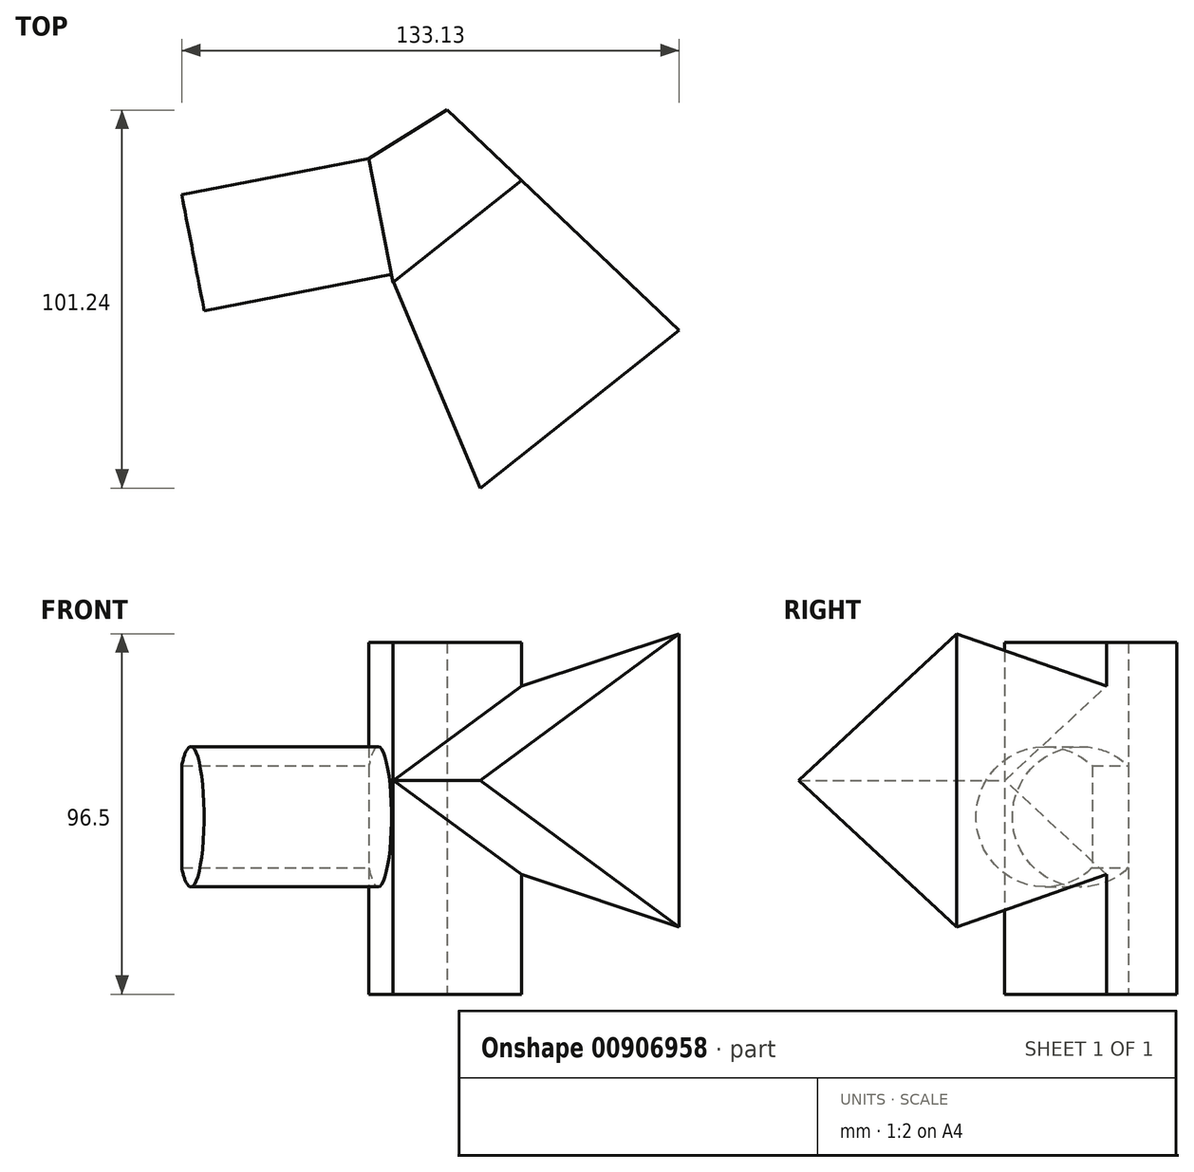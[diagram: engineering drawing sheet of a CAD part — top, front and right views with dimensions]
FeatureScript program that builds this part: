
annotation { "Feature Type Name" : "Feature", "Feature Type Description" : "" }
export const myFeature = defineFeature(function(context is Context, id is Id, definition is map)
    precondition{}
    {
        {
            var Q0;
            Q0=qCreatedBy(makeId("Top.planeOp"),FACE);
            var sketch = newSketch(context, id + "F0", { "sketchPlane" : qUnion([Q0])});
            skLineSegment(sketch, "E0", {"start": v(-14.54, -24.13) * mm, "end": v(-20.96, 9.05) * mm});
            skLineSegment(sketch, "E1", {"start": v(-20.96, 9.05) * mm, "end": v(0, 22.03) * mm});
            skLineSegment(sketch, "E2", {"start": v(-14.54, -24.13) * mm, "end": v(19.84, 3.17) * mm});
            skLineSegment(sketch, "E3", {"start": v(19.84, 3.17) * mm, "end": v(0, 22.03) * mm});
            skSolve(sketch);
        }
        {
            var Q0;
            Q0=makeQuery(id+"F0.imprint","IMPRINT",FACE,{"disambiguationData":[TD([[makeQuery(id+"F0.imprint","IMPRINT",EDGE,{"derivedFrom":sQuery(id+"F0.wireOp",EDGE,"E0")}),-1.0]])]});
            extrude(context, id + "F1", {"entities" : qUnion([Q0]), "depth" : 50.3 * mm, "offsetDistance" : 25.4 * mm, "hasSecondDirection" : true, "secondDirectionOppositeDirection" : true, "secondDirectionDepth" : 43.94 * mm});
        }
        {
            var Q0;
            Q0=makeQuery(id+"F1.opExtrude","SWEPT_FACE",FACE,{"disambiguationData":[OSD([sQuery(id+"F0.wireOp",EDGE,"E0")])]});
            var sketch = newSketch(context, id + "F2", { "sketchPlane" : qUnion([Q0])});
            skCircle(sketch, "E4", {"center": v(0, 3.56) * mm, "radius": 18.77 * mm});
            skSolve(sketch);
        }
        {
            var Q0;
            {var subQ0=sQuery(id+"F2.wireOp",EDGE,"E4");var subQ1=makeQuery(id+"F1.opExtrude","SWEPT_EDGE",EDGE,{"disambiguationData":[OSD([sQuery(id+"F0.wireOp",EDGE,"E0"),sQuery(id+"F0.wireOp",EDGE,"E1")])]});var subQ2=makeQuery(id+"F2.imprint","INTERSECT",VERTEX,{"disambiguationData":[OD(0.0)],"derivedFrom":[subQ1,subQ0]});Q0=makeQuery(id+"F2.imprint","IMPRINT",FACE,{"disambiguationData":[TD([[makeQuery(id+"F2.imprint","IMPRINT",EDGE,{"disambiguationData":[TD([[subQ2,-1.0]])],"derivedFrom":subQ0}),1.0]])]});}
            extrude(context, id + "F3", {"entities" : qUnion([Q0]), "operationType" : NewBodyOperationType.ADD, "depth" : 51.05 * mm, "offsetDistance" : 25.4 * mm});
        }
        {
            var Q0;
            Q0=makeQuery(id+"F1.opExtrude","SWEPT_FACE",FACE,{"disambiguationData":[OSD([sQuery(id+"F0.wireOp",EDGE,"E2")])]});
            var sketch = newSketch(context, id + "F4", { "sketchPlane" : qUnion([Q0])});
            skCircle(sketch, "E5.cCircle", {"center": v(2.96, 13.32) * mm, "radius": 14.55 * mm, "construction": true});
            skLineSegment(sketch, "E5.0", {"start": v(17.5, 38.52) * mm, "end": v(17.5, -11.88) * mm});
            skLineSegment(sketch, "E5.1", {"start": v(17.5, -11.88) * mm, "end": v(-26.15, 13.32) * mm});
            skLineSegment(sketch, "E5.2", {"start": v(-26.15, 13.32) * mm, "end": v(17.5, 38.52) * mm});
            skPoint(sketch, "E5.0.midPoint", {"position": v(17.5, 13.32) * mm});
            skSolve(sketch);
        }
        {
            var Q0;
            Q0=makeQuery(id+"F4.imprint","IMPRINT",FACE,{"disambiguationData":[TD([[makeQuery(id+"F4.imprint","IMPRINT",EDGE,{"derivedFrom":sQuery(id+"F4.wireOp",EDGE,"E5.0")}),-1.0]])]});
            extrude(context, id + "F5", {"entities" : qUnion([Q0]), "operationType" : NewBodyOperationType.ADD, "depth" : 57.66 * mm, "offsetDistance" : 25.4 * mm, "hasDraft" : true, "draftAngle" : 8 * degree});
        }
    });
